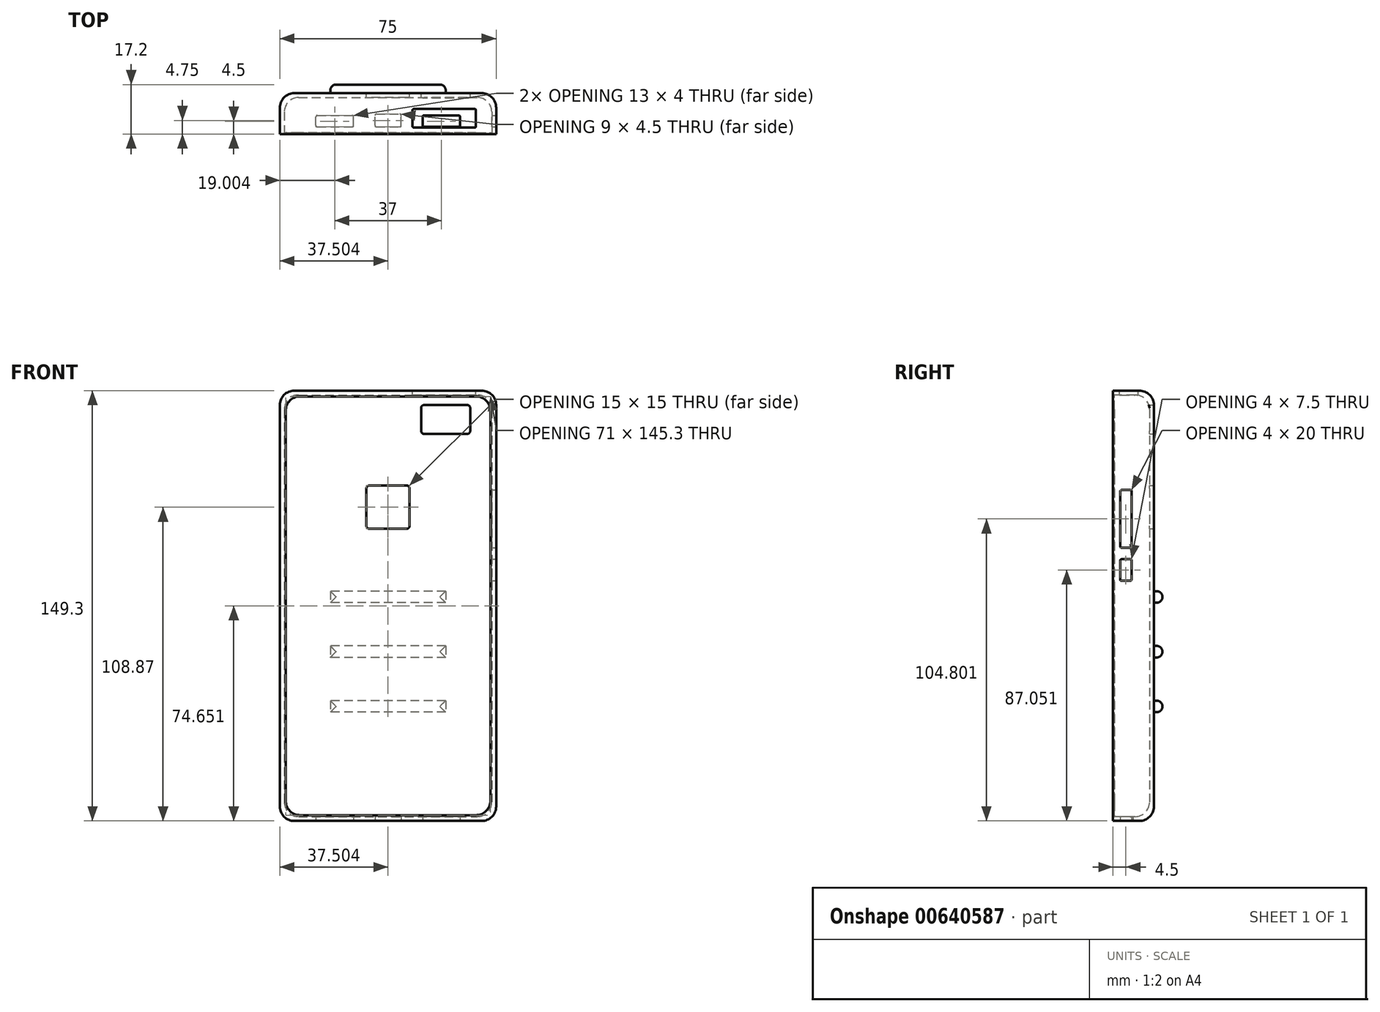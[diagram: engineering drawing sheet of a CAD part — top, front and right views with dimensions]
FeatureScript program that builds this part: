
annotation { "Feature Type Name" : "Feature", "Feature Type Description" : "" }
export const myFeature = defineFeature(function(context is Context, id is Id, definition is map)
    precondition{}
    {
        {
            var Q0;
            Q0=qCreatedBy(makeId("Front.planeOp"),FACE);
            var sketch = newSketch(context, id + "F0", { "sketchPlane" : qUnion([Q0])});
            skLineSegment(sketch, "E0.bottom", {"start": v(-56.12, 78.07) * mm, "end": v(18.88, 78.07) * mm});
            skLineSegment(sketch, "E0.top", {"start": v(-56.12, -71.23) * mm, "end": v(18.88, -71.23) * mm});
            skLineSegment(sketch, "E0.left", {"start": v(-56.12, 78.07) * mm, "end": v(-56.12, -71.23) * mm});
            skLineSegment(sketch, "E0.right", {"start": v(18.88, 78.07) * mm, "end": v(18.88, -71.23) * mm});
            skLineSegment(sketch, "E1", {"start": v(-55.06, -70.03) * mm, "end": v(-56.12, -71.23) * mm, "construction": true});
            skLineSegment(sketch, "E2", {"start": v(17.94, 76.77) * mm, "end": v(18.88, 78.07) * mm, "construction": true});
            skSolve(sketch);
        }
        {
            var Q0;
            Q0=makeQuery(id+"F0.imprint","IMPRINT",FACE,{"disambiguationData":[TD([[makeQuery(id+"F0.imprint","IMPRINT",EDGE,{"derivedFrom":sQuery(id+"F0.wireOp",EDGE,"E0.bottom")}),-1.0]])]});
            extrude(context, id + "F1", {"entities" : qUnion([Q0]), "depth" : -1.5 * mm, "offsetDistance" : 25 * mm});
        }
        {
            var Q0;
            Q0=makeQuery(id+"F1.opExtrude","CAP_FACE",FACE,{"disambiguationData":[OSD([sQuery(id+"F0.wireOp",EDGE,"E0.bottom"),sQuery(id+"F0.wireOp",EDGE,"E0.top"),sQuery(id+"F0.wireOp",EDGE,"E0.left"),sQuery(id+"F0.wireOp",EDGE,"E0.right")])],"isStart":true});
            extrude(context, id + "F2", {"entities" : qUnion([Q0]), "operationType" : NewBodyOperationType.ADD, "depth" : 12.2 * mm, "offsetDistance" : 25 * mm});
        }
        {
            var Q0;
            Q0=makeQuery(id+"F2.opExtrude","CAP_FACE",FACE,{"disambiguationData":[OSD([sQuery(id+"F0.wireOp",EDGE,"E0.bottom"),sQuery(id+"F0.wireOp",EDGE,"E0.top"),sQuery(id+"F0.wireOp",EDGE,"E0.left"),sQuery(id+"F0.wireOp",EDGE,"E0.right")])],"isStart":false});
            shell(context, id + "F3", {"entities" : qUnion([Q0]), "thickness" : 1.5 * mm});
        }
        {
            var Q0;
            {var subQ0=sQuery(id+"F0.wireOp",EDGE,"E0.top");Q0=makeQuery(id+"F2.boolean.opBoolean","MERGE",FACE,{"derivedFrom":[makeQuery(id+"F1.opExtrude","SWEPT_FACE",FACE,{"disambiguationData":[OSD([subQ0])]}),makeQuery(id+"F2.opExtrude","SWEPT_FACE",FACE,{"disambiguationData":[OSD([subQ0])]})]});}
            var sketch = newSketch(context, id + "F4", { "sketchPlane" : qUnion([Q0])});
            skLineSegment(sketch, "E3.bottom", {"start": v(-43.62, 10.2) * mm, "end": v(-30.62, 10.2) * mm});
            skLineSegment(sketch, "E3.top", {"start": v(-43.62, 6.2) * mm, "end": v(-30.62, 6.2) * mm});
            skLineSegment(sketch, "E3.left", {"start": v(-43.62, 10.2) * mm, "end": v(-43.62, 6.2) * mm});
            skLineSegment(sketch, "E3.right", {"start": v(-30.62, 10.2) * mm, "end": v(-30.62, 6.2) * mm});
            skLineSegment(sketch, "E4.bottom", {"start": v(-23.12, 10.2) * mm, "end": v(-14.12, 10.2) * mm});
            skLineSegment(sketch, "E4.top", {"start": v(-23.12, 5.7) * mm, "end": v(-14.12, 5.7) * mm});
            skLineSegment(sketch, "E4.left", {"start": v(-23.12, 10.2) * mm, "end": v(-23.12, 5.7) * mm});
            skLineSegment(sketch, "E4.right", {"start": v(-14.12, 10.2) * mm, "end": v(-14.12, 5.7) * mm});
            skLineSegment(sketch, "E5.bottom", {"start": v(-6.62, 10.2) * mm, "end": v(6.38, 10.2) * mm});
            skLineSegment(sketch, "E5.top", {"start": v(-6.62, 6.2) * mm, "end": v(6.38, 6.2) * mm});
            skLineSegment(sketch, "E5.left", {"start": v(-6.62, 10.2) * mm, "end": v(-6.62, 6.2) * mm});
            skLineSegment(sketch, "E5.right", {"start": v(6.38, 10.2) * mm, "end": v(6.38, 6.2) * mm});
            skLineSegment(sketch, "E6", {"start": v(-30.62, 10.2) * mm, "end": v(-23.12, 10.2) * mm, "construction": true});
            skLineSegment(sketch, "E7", {"start": v(-14.12, 10.2) * mm, "end": v(-6.62, 10.2) * mm, "construction": true});
            skLineSegment(sketch, "E8", {"start": v(-30.58, 10.2) * mm, "end": v(-30.58, 12.2) * mm, "construction": true});
            skLineSegment(sketch, "E9", {"start": v(6.38, 8.2) * mm, "end": v(18.88, 8.2) * mm, "construction": true});
            skLineSegment(sketch, "E10", {"start": v(-43.62, 8.2) * mm, "end": v(-56.12, 8.2) * mm, "construction": true});
            skSolve(sketch);
        }
        {
            var Q0;
            Q0=makeQuery(id+"F4.imprint","IMPRINT",FACE,{"disambiguationData":[TD([[makeQuery(id+"F4.imprint","IMPRINT",EDGE,{"derivedFrom":sQuery(id+"F4.wireOp",EDGE,"E3.bottom")}),-1.0]])]});
            var Q1;
            Q1=makeQuery(id+"F4.imprint","IMPRINT",FACE,{"disambiguationData":[TD([[makeQuery(id+"F4.imprint","IMPRINT",EDGE,{"derivedFrom":sQuery(id+"F4.wireOp",EDGE,"E4.bottom")}),-1.0]])]});
            var Q2;
            Q2=makeQuery(id+"F4.imprint","IMPRINT",FACE,{"disambiguationData":[TD([[makeQuery(id+"F4.imprint","IMPRINT",EDGE,{"derivedFrom":sQuery(id+"F4.wireOp",EDGE,"E5.bottom")}),-1.0]])]});
            var Q3;
            Q3=makeQuery(id+"F3.opShell","OFFSET_FACE",FACE,{"disambiguationData":[OSD([sQuery(id+"F0.wireOp",EDGE,"E0.top")])]});
            extrude(context, id + "F5", {"entities" : qUnion([Q0, Q1, Q2]), "operationType" : NewBodyOperationType.REMOVE, "endBound" : BoundingType.UP_TO_SURFACE, "oppositeDirection" : true, "depth" : 25 * mm, "endBoundEntityFace" : qUnion([Q3]), "offsetDistance" : 25 * mm});
        }
        {
            var Q0;
            Q0=makeQuery(id+"F5.boolean.opBoolean","COPY",EDGE,{"derivedFrom":makeQuery(id+"F5.opExtrude","SWEPT_EDGE",EDGE,{"disambiguationData":[OSD([sQuery(id+"F4.wireOp",EDGE,"E4.top"),sQuery(id+"F4.wireOp",EDGE,"E4.left")])]})});
            var Q1;
            Q1=makeQuery(id+"F5.boolean.opBoolean","COPY",EDGE,{"derivedFrom":makeQuery(id+"F5.opExtrude","SWEPT_EDGE",EDGE,{"disambiguationData":[OSD([sQuery(id+"F4.wireOp",EDGE,"E3.top"),sQuery(id+"F4.wireOp",EDGE,"E3.left")])]})});
            var Q2;
            Q2=makeQuery(id+"F5.boolean.opBoolean","COPY",EDGE,{"derivedFrom":makeQuery(id+"F5.opExtrude","SWEPT_EDGE",EDGE,{"disambiguationData":[OSD([sQuery(id+"F4.wireOp",EDGE,"E3.top"),sQuery(id+"F4.wireOp",EDGE,"E3.right")])]})});
            var Q3;
            Q3=makeQuery(id+"F5.boolean.opBoolean","COPY",EDGE,{"derivedFrom":makeQuery(id+"F5.opExtrude","SWEPT_EDGE",EDGE,{"disambiguationData":[OSD([sQuery(id+"F4.wireOp",EDGE,"E3.bottom"),sQuery(id+"F4.wireOp",EDGE,"E3.right")])]})});
            var Q4;
            Q4=makeQuery(id+"F5.boolean.opBoolean","COPY",EDGE,{"derivedFrom":makeQuery(id+"F5.opExtrude","SWEPT_EDGE",EDGE,{"disambiguationData":[OSD([sQuery(id+"F4.wireOp",EDGE,"E3.bottom"),sQuery(id+"F4.wireOp",EDGE,"E3.left")])]})});
            var Q5;
            Q5=makeQuery(id+"F5.boolean.opBoolean","COPY",EDGE,{"derivedFrom":makeQuery(id+"F5.opExtrude","CAP_EDGE",EDGE,{"disambiguationData":[OSD([sQuery(id+"F4.wireOp",EDGE,"E3.top")])],"isStart":true})});
            var Q6;
            Q6=makeQuery(id+"F5.boolean.opBoolean","COPY",EDGE,{"derivedFrom":makeQuery(id+"F5.opExtrude","SWEPT_EDGE",EDGE,{"disambiguationData":[OSD([sQuery(id+"F4.wireOp",EDGE,"E4.top"),sQuery(id+"F4.wireOp",EDGE,"E4.right")])]})});
            var Q7;
            Q7=makeQuery(id+"F5.boolean.opBoolean","COPY",EDGE,{"derivedFrom":makeQuery(id+"F5.opExtrude","SWEPT_EDGE",EDGE,{"disambiguationData":[OSD([sQuery(id+"F4.wireOp",EDGE,"E4.bottom"),sQuery(id+"F4.wireOp",EDGE,"E4.right")])]})});
            var Q8;
            Q8=makeQuery(id+"F5.boolean.opBoolean","COPY",EDGE,{"derivedFrom":makeQuery(id+"F5.opExtrude","SWEPT_EDGE",EDGE,{"disambiguationData":[OSD([sQuery(id+"F4.wireOp",EDGE,"E4.bottom"),sQuery(id+"F4.wireOp",EDGE,"E4.left")])]})});
            var Q9;
            Q9=makeQuery(id+"F5.boolean.opBoolean","COPY",EDGE,{"derivedFrom":makeQuery(id+"F5.opExtrude","CAP_EDGE",EDGE,{"disambiguationData":[OSD([sQuery(id+"F4.wireOp",EDGE,"E4.bottom")])],"isStart":true})});
            var Q10;
            Q10=makeQuery(id+"F5.boolean.opBoolean","COPY",EDGE,{"derivedFrom":makeQuery(id+"F5.opExtrude","SWEPT_EDGE",EDGE,{"disambiguationData":[OSD([sQuery(id+"F4.wireOp",EDGE,"E5.bottom"),sQuery(id+"F4.wireOp",EDGE,"E5.left")])]})});
            var Q11;
            Q11=makeQuery(id+"F5.boolean.opBoolean","COPY",EDGE,{"derivedFrom":makeQuery(id+"F5.opExtrude","CAP_EDGE",EDGE,{"disambiguationData":[OSD([sQuery(id+"F4.wireOp",EDGE,"E5.left")])],"isStart":true})});
            var Q12;
            Q12=makeQuery(id+"F5.boolean.opBoolean","COPY",EDGE,{"derivedFrom":makeQuery(id+"F5.opExtrude","SWEPT_EDGE",EDGE,{"disambiguationData":[OSD([sQuery(id+"F4.wireOp",EDGE,"E5.top"),sQuery(id+"F4.wireOp",EDGE,"E5.left")])]})});
            var Q13;
            Q13=makeQuery(id+"F5.boolean.opBoolean","COPY",EDGE,{"derivedFrom":makeQuery(id+"F5.opExtrude","SWEPT_EDGE",EDGE,{"disambiguationData":[OSD([sQuery(id+"F4.wireOp",EDGE,"E5.top"),sQuery(id+"F4.wireOp",EDGE,"E5.right")])]})});
            var Q14;
            Q14=makeQuery(id+"F5.boolean.opBoolean","COPY",EDGE,{"derivedFrom":makeQuery(id+"F5.opExtrude","SWEPT_EDGE",EDGE,{"disambiguationData":[OSD([sQuery(id+"F4.wireOp",EDGE,"E5.bottom"),sQuery(id+"F4.wireOp",EDGE,"E5.right")])]})});
            fillet(context, id + "F6", {"entities" : qUnion([Q0, Q1, Q2, Q3, Q4, Q5, Q6, Q7, Q8, Q9, Q10, Q11, Q12, Q13, Q14]), "radius" : 0.5 * mm, "tangentPropagation" : true, "allowEdgeOverflow" : false});
        }
        {
            var Q0;
            {var subQ0=sQuery(id+"F0.wireOp",EDGE,"E0.right");Q0=makeQuery(id+"F2.boolean.opBoolean","MERGE",FACE,{"derivedFrom":[makeQuery(id+"F1.opExtrude","SWEPT_FACE",FACE,{"disambiguationData":[OSD([subQ0])]}),makeQuery(id+"F2.opExtrude","SWEPT_FACE",FACE,{"disambiguationData":[OSD([subQ0])]})]});}
            var sketch = newSketch(context, id + "F7", { "sketchPlane" : qUnion([Q0])});
            skLineSegment(sketch, "E11.bottom", {"start": v(-10.2, 23.57) * mm, "end": v(-6.2, 23.57) * mm});
            skLineSegment(sketch, "E11.top", {"start": v(-10.2, 43.57) * mm, "end": v(-6.2, 43.57) * mm});
            skLineSegment(sketch, "E11.left", {"start": v(-10.2, 23.57) * mm, "end": v(-10.2, 43.57) * mm});
            skLineSegment(sketch, "E11.right", {"start": v(-6.2, 23.57) * mm, "end": v(-6.2, 43.57) * mm});
            skLineSegment(sketch, "E12", {"start": v(-8.2, 43.57) * mm, "end": v(-8.2, 78.07) * mm, "construction": true});
            skLineSegment(sketch, "E13.bottom", {"start": v(-10.2, 12.07) * mm, "end": v(-6.2, 12.07) * mm});
            skLineSegment(sketch, "E13.top", {"start": v(-10.2, 19.57) * mm, "end": v(-6.2, 19.57) * mm});
            skLineSegment(sketch, "E13.left", {"start": v(-10.2, 12.07) * mm, "end": v(-10.2, 19.57) * mm});
            skLineSegment(sketch, "E13.right", {"start": v(-6.2, 12.07) * mm, "end": v(-6.2, 19.57) * mm});
            skLineSegment(sketch, "E14", {"start": v(-10.2, 19.57) * mm, "end": v(-10.2, 23.57) * mm, "construction": true});
            skSolve(sketch);
        }
        {
            var Q0;
            {var subQ0=sQuery(id+"F0.wireOp",EDGE,"E0.bottom");Q0=makeQuery(id+"F2.boolean.opBoolean","MERGE",FACE,{"derivedFrom":[makeQuery(id+"F1.opExtrude","SWEPT_FACE",FACE,{"disambiguationData":[OSD([subQ0])]}),makeQuery(id+"F2.opExtrude","SWEPT_FACE",FACE,{"disambiguationData":[OSD([subQ0])]})]});}
            var sketch = newSketch(context, id + "F8", { "sketchPlane" : qUnion([Q0])});
            skLineSegment(sketch, "E15.bottom", {"start": v(11.88, -10.45) * mm, "end": v(-10.12, -10.45) * mm});
            skLineSegment(sketch, "E15.top", {"start": v(11.88, -3.95) * mm, "end": v(-10.12, -3.95) * mm});
            skLineSegment(sketch, "E15.left", {"start": v(11.88, -10.45) * mm, "end": v(11.88, -3.95) * mm});
            skLineSegment(sketch, "E15.right", {"start": v(-10.12, -10.45) * mm, "end": v(-10.12, -3.95) * mm});
            skSolve(sketch);
        }
        {
            var Q0;
            Q0=makeQuery(id+"F8.imprint","IMPRINT",FACE,{"disambiguationData":[TD([[makeQuery(id+"F8.imprint","IMPRINT",EDGE,{"derivedFrom":sQuery(id+"F8.wireOp",EDGE,"E15.bottom")}),-1.0]])]});
            var Q1;
            Q1=makeQuery(id+"F3.opShell","OFFSET_FACE",FACE,{"disambiguationData":[OSD([sQuery(id+"F0.wireOp",EDGE,"E0.bottom")])]});
            extrude(context, id + "F9", {"entities" : qUnion([Q0]), "operationType" : NewBodyOperationType.REMOVE, "endBound" : BoundingType.UP_TO_SURFACE, "oppositeDirection" : true, "depth" : 25 * mm, "endBoundEntityFace" : qUnion([Q1]), "offsetDistance" : 25 * mm});
        }
        {
            var Q0;
            Q0=makeQuery(id+"F9.boolean.opBoolean","COPY",EDGE,{"derivedFrom":makeQuery(id+"F9.opExtrude","SWEPT_EDGE",EDGE,{"disambiguationData":[OSD([sQuery(id+"F8.wireOp",EDGE,"E15.top"),sQuery(id+"F8.wireOp",EDGE,"E15.left")])]})});
            var Q1;
            Q1=makeQuery(id+"F9.boolean.opBoolean","COPY",EDGE,{"derivedFrom":makeQuery(id+"F9.opExtrude","SWEPT_EDGE",EDGE,{"disambiguationData":[OSD([sQuery(id+"F8.wireOp",EDGE,"E15.bottom"),sQuery(id+"F8.wireOp",EDGE,"E15.left")])]})});
            var Q2;
            Q2=makeQuery(id+"F9.boolean.opBoolean","COPY",EDGE,{"derivedFrom":makeQuery(id+"F9.opExtrude","CAP_EDGE",EDGE,{"disambiguationData":[OSD([sQuery(id+"F8.wireOp",EDGE,"E15.right")])],"isStart":true})});
            var Q3;
            Q3=makeQuery(id+"F9.boolean.opBoolean","COPY",EDGE,{"derivedFrom":makeQuery(id+"F9.opExtrude","SWEPT_EDGE",EDGE,{"disambiguationData":[OSD([sQuery(id+"F8.wireOp",EDGE,"E15.top"),sQuery(id+"F8.wireOp",EDGE,"E15.right")])]})});
            var Q4;
            Q4=makeQuery(id+"F9.boolean.opBoolean","COPY",EDGE,{"derivedFrom":makeQuery(id+"F9.opExtrude","SWEPT_EDGE",EDGE,{"disambiguationData":[OSD([sQuery(id+"F8.wireOp",EDGE,"E15.bottom"),sQuery(id+"F8.wireOp",EDGE,"E15.right")])]})});
            fillet(context, id + "F10", {"entities" : qUnion([Q0, Q1, Q2, Q3, Q4]), "radius" : 0.5 * mm, "tangentPropagation" : true, "allowEdgeOverflow" : false});
        }
        {
            var Q0;
            Q0=makeQuery(id+"F7.imprint","IMPRINT",FACE,{"disambiguationData":[TD([[makeQuery(id+"F7.imprint","IMPRINT",EDGE,{"derivedFrom":sQuery(id+"F7.wireOp",EDGE,"E11.bottom")}),1.0]])]});
            var Q1;
            Q1=makeQuery(id+"F7.imprint","IMPRINT",FACE,{"disambiguationData":[TD([[makeQuery(id+"F7.imprint","IMPRINT",EDGE,{"derivedFrom":sQuery(id+"F7.wireOp",EDGE,"E13.bottom")}),1.0]])]});
            var Q2;
            Q2=makeQuery(id+"F3.opShell","OFFSET_FACE",FACE,{"disambiguationData":[OSD([sQuery(id+"F0.wireOp",EDGE,"E0.right")])]});
            extrude(context, id + "F11", {"entities" : qUnion([Q0, Q1]), "operationType" : NewBodyOperationType.REMOVE, "endBound" : BoundingType.UP_TO_SURFACE, "oppositeDirection" : true, "depth" : 25 * mm, "endBoundEntityFace" : qUnion([Q2]), "offsetDistance" : 25 * mm});
        }
        {
            var Q0;
            Q0=makeQuery(id+"F11.boolean.opBoolean","COPY",EDGE,{"derivedFrom":makeQuery(id+"F11.opExtrude","SWEPT_EDGE",EDGE,{"disambiguationData":[OSD([sQuery(id+"F7.wireOp",EDGE,"E13.bottom"),sQuery(id+"F7.wireOp",EDGE,"E13.right")])]})});
            var Q1;
            Q1=makeQuery(id+"F11.boolean.opBoolean","COPY",EDGE,{"derivedFrom":makeQuery(id+"F11.opExtrude","SWEPT_EDGE",EDGE,{"disambiguationData":[OSD([sQuery(id+"F7.wireOp",EDGE,"E11.bottom"),sQuery(id+"F7.wireOp",EDGE,"E11.right")])]})});
            var Q2;
            Q2=makeQuery(id+"F11.boolean.opBoolean","COPY",EDGE,{"derivedFrom":makeQuery(id+"F11.opExtrude","SWEPT_EDGE",EDGE,{"disambiguationData":[OSD([sQuery(id+"F7.wireOp",EDGE,"E13.bottom"),sQuery(id+"F7.wireOp",EDGE,"E13.left")])]})});
            var Q3;
            Q3=makeQuery(id+"F11.boolean.opBoolean","COPY",EDGE,{"derivedFrom":makeQuery(id+"F11.opExtrude","SWEPT_EDGE",EDGE,{"disambiguationData":[OSD([sQuery(id+"F7.wireOp",EDGE,"E11.bottom"),sQuery(id+"F7.wireOp",EDGE,"E11.left")])]})});
            var Q4;
            Q4=makeQuery(id+"F11.boolean.opBoolean","COPY",EDGE,{"derivedFrom":makeQuery(id+"F11.opExtrude","SWEPT_EDGE",EDGE,{"disambiguationData":[OSD([sQuery(id+"F7.wireOp",EDGE,"E13.top"),sQuery(id+"F7.wireOp",EDGE,"E13.right")])]})});
            var Q5;
            Q5=makeQuery(id+"F11.boolean.opBoolean","COPY",EDGE,{"derivedFrom":makeQuery(id+"F11.opExtrude","SWEPT_EDGE",EDGE,{"disambiguationData":[OSD([sQuery(id+"F7.wireOp",EDGE,"E11.top"),sQuery(id+"F7.wireOp",EDGE,"E11.right")])]})});
            var Q6;
            Q6=makeQuery(id+"F11.boolean.opBoolean","COPY",EDGE,{"derivedFrom":makeQuery(id+"F11.opExtrude","CAP_EDGE",EDGE,{"disambiguationData":[OSD([sQuery(id+"F7.wireOp",EDGE,"E11.left")])],"isStart":true})});
            var Q7;
            Q7=makeQuery(id+"F11.boolean.opBoolean","COPY",EDGE,{"derivedFrom":makeQuery(id+"F11.opExtrude","SWEPT_EDGE",EDGE,{"disambiguationData":[OSD([sQuery(id+"F7.wireOp",EDGE,"E11.top"),sQuery(id+"F7.wireOp",EDGE,"E11.left")])]})});
            var Q8;
            Q8=makeQuery(id+"F11.boolean.opBoolean","COPY",EDGE,{"derivedFrom":makeQuery(id+"F11.opExtrude","SWEPT_EDGE",EDGE,{"disambiguationData":[OSD([sQuery(id+"F7.wireOp",EDGE,"E13.top"),sQuery(id+"F7.wireOp",EDGE,"E13.left")])]})});
            var Q9;
            Q9=makeQuery(id+"F11.boolean.opBoolean","COPY",EDGE,{"derivedFrom":makeQuery(id+"F11.opExtrude","CAP_EDGE",EDGE,{"disambiguationData":[OSD([sQuery(id+"F7.wireOp",EDGE,"E13.left")])],"isStart":true})});
            fillet(context, id + "F12", {"entities" : qUnion([Q0, Q1, Q2, Q3, Q4, Q5, Q6, Q7, Q8, Q9]), "radius" : 0.5 * mm, "tangentPropagation" : true, "allowEdgeOverflow" : false});
        }
        {
            var Q0;
            Q0=makeQuery(id+"F1.opExtrude","CAP_FACE",FACE,{"disambiguationData":[OSD([sQuery(id+"F0.wireOp",EDGE,"E0.bottom"),sQuery(id+"F0.wireOp",EDGE,"E0.top"),sQuery(id+"F0.wireOp",EDGE,"E0.left"),sQuery(id+"F0.wireOp",EDGE,"E0.right")])],"isStart":false});
            var sketch = newSketch(context, id + "F13", { "sketchPlane" : qUnion([Q0])});
            skLineSegment(sketch, "E16.bottom", {"start": v(-9.88, 73.07) * mm, "end": v(7.12, 73.07) * mm});
            skLineSegment(sketch, "E16.top", {"start": v(-9.88, 63.07) * mm, "end": v(7.12, 63.07) * mm});
            skLineSegment(sketch, "E16.left", {"start": v(-9.88, 73.07) * mm, "end": v(-9.88, 63.07) * mm});
            skLineSegment(sketch, "E16.right", {"start": v(7.12, 73.07) * mm, "end": v(7.12, 63.07) * mm});
            skLineSegment(sketch, "E17.bottom", {"start": v(11.12, 45.14) * mm, "end": v(26.12, 45.14) * mm});
            skLineSegment(sketch, "E17.top", {"start": v(11.12, 30.14) * mm, "end": v(26.12, 30.14) * mm});
            skLineSegment(sketch, "E17.left", {"start": v(11.12, 45.14) * mm, "end": v(11.12, 30.14) * mm});
            skLineSegment(sketch, "E17.right", {"start": v(26.12, 45.14) * mm, "end": v(26.12, 30.14) * mm});
            skSolve(sketch);
        }
        {
            var Q0;
            Q0=makeQuery(id+"F13.imprint","IMPRINT",FACE,{"disambiguationData":[TD([[makeQuery(id+"F13.imprint","IMPRINT",EDGE,{"derivedFrom":sQuery(id+"F13.wireOp",EDGE,"E17.bottom")}),-1.0]])]});
            var Q1;
            Q1=makeQuery(id+"F13.imprint","IMPRINT",FACE,{"disambiguationData":[TD([[makeQuery(id+"F13.imprint","IMPRINT",EDGE,{"derivedFrom":sQuery(id+"F13.wireOp",EDGE,"E16.bottom")}),-1.0]])]});
            var Q2;
            Q2=makeQuery(id+"F3.opShell","OFFSET_FACE",FACE,{"disambiguationData":[OSD([sQuery(id+"F0.wireOp",EDGE,"E0.bottom"),sQuery(id+"F0.wireOp",EDGE,"E0.top"),sQuery(id+"F0.wireOp",EDGE,"E0.left"),sQuery(id+"F0.wireOp",EDGE,"E0.right")])]});
            extrude(context, id + "F14", {"entities" : qUnion([Q0, Q1]), "operationType" : NewBodyOperationType.REMOVE, "endBound" : BoundingType.UP_TO_SURFACE, "oppositeDirection" : true, "depth" : 25 * mm, "endBoundEntityFace" : qUnion([Q2]), "offsetDistance" : 25 * mm});
        }
        {
            var Q0;
            Q0=makeQuery(id+"F14.boolean.opBoolean","COPY",EDGE,{"derivedFrom":makeQuery(id+"F14.opExtrude","SWEPT_EDGE",EDGE,{"disambiguationData":[OSD([sQuery(id+"F13.wireOp",EDGE,"E16.top"),sQuery(id+"F13.wireOp",EDGE,"E16.left")])]})});
            var Q1;
            Q1=makeQuery(id+"F14.boolean.opBoolean","COPY",EDGE,{"derivedFrom":makeQuery(id+"F14.opExtrude","SWEPT_EDGE",EDGE,{"disambiguationData":[OSD([sQuery(id+"F13.wireOp",EDGE,"E16.top"),sQuery(id+"F13.wireOp",EDGE,"E16.right")])]})});
            var Q2;
            Q2=makeQuery(id+"F14.boolean.opBoolean","COPY",EDGE,{"derivedFrom":makeQuery(id+"F14.opExtrude","SWEPT_EDGE",EDGE,{"disambiguationData":[OSD([sQuery(id+"F13.wireOp",EDGE,"E16.bottom"),sQuery(id+"F13.wireOp",EDGE,"E16.right")])]})});
            var Q3;
            Q3=makeQuery(id+"F14.boolean.opBoolean","COPY",EDGE,{"derivedFrom":makeQuery(id+"F14.opExtrude","SWEPT_EDGE",EDGE,{"disambiguationData":[OSD([sQuery(id+"F13.wireOp",EDGE,"E16.bottom"),sQuery(id+"F13.wireOp",EDGE,"E16.left")])]})});
            var Q4;
            Q4=makeQuery(id+"F14.boolean.opBoolean","COPY",EDGE,{"derivedFrom":makeQuery(id+"F14.opExtrude","CAP_EDGE",EDGE,{"disambiguationData":[OSD([sQuery(id+"F13.wireOp",EDGE,"E16.bottom")])],"isStart":true})});
            var Q5;
            Q5=makeQuery(id+"F14.boolean.opBoolean","COPY",EDGE,{"derivedFrom":makeQuery(id+"F14.opExtrude","SWEPT_EDGE",EDGE,{"disambiguationData":[OSD([sQuery(id+"F13.wireOp",EDGE,"E17.top"),sQuery(id+"F13.wireOp",EDGE,"E17.left")])]})});
            var Q6;
            Q6=makeQuery(id+"F14.boolean.opBoolean","COPY",EDGE,{"derivedFrom":makeQuery(id+"F14.opExtrude","SWEPT_EDGE",EDGE,{"disambiguationData":[OSD([sQuery(id+"F13.wireOp",EDGE,"E17.bottom"),sQuery(id+"F13.wireOp",EDGE,"E17.left")])]})});
            var Q7;
            Q7=makeQuery(id+"F14.boolean.opBoolean","COPY",EDGE,{"derivedFrom":makeQuery(id+"F14.opExtrude","SWEPT_EDGE",EDGE,{"disambiguationData":[OSD([sQuery(id+"F13.wireOp",EDGE,"E17.bottom"),sQuery(id+"F13.wireOp",EDGE,"E17.right")])]})});
            var Q8;
            Q8=makeQuery(id+"F14.boolean.opBoolean","COPY",EDGE,{"derivedFrom":makeQuery(id+"F14.opExtrude","SWEPT_EDGE",EDGE,{"disambiguationData":[OSD([sQuery(id+"F13.wireOp",EDGE,"E17.top"),sQuery(id+"F13.wireOp",EDGE,"E17.right")])]})});
            var Q9;
            Q9=makeQuery(id+"F14.boolean.opBoolean","COPY",EDGE,{"derivedFrom":makeQuery(id+"F14.opExtrude","CAP_EDGE",EDGE,{"disambiguationData":[OSD([sQuery(id+"F13.wireOp",EDGE,"E17.right")])],"isStart":true})});
            fillet(context, id + "F15", {"entities" : qUnion([Q0, Q1, Q2, Q3, Q4, Q5, Q6, Q7, Q8, Q9]), "radius" : 1 * mm, "tangentPropagation" : true, "allowEdgeOverflow" : false});
        }
        {
            var Q0;
            Q0=makeQuery(id+"F1.opExtrude","CAP_EDGE",EDGE,{"disambiguationData":[OSD([sQuery(id+"F0.wireOp",EDGE,"E0.top")])],"isStart":false});
            fillet(context, id + "F16", {"entities" : qUnion([Q0]), "radius" : 5 * mm, "tangentPropagation" : true, "allowEdgeOverflow" : false});
        }
        {
            var Q0;
            Q0=makeQuery(id+"F2.opExtrude","CAP_FACE",FACE,{"disambiguationData":[OSD([sQuery(id+"F0.wireOp",EDGE,"E0.bottom"),sQuery(id+"F0.wireOp",EDGE,"E0.top"),sQuery(id+"F0.wireOp",EDGE,"E0.left"),sQuery(id+"F0.wireOp",EDGE,"E0.right")])],"isStart":false});
            var sketch = newSketch(context, id + "F17", { "sketchPlane" : qUnion([Q0])});
            skLineSegment(sketch, "E18.bottom", {"start": v(-56.12, 78.07) * mm, "end": v(18.88, 78.07) * mm});
            skLineSegment(sketch, "E18.top", {"start": v(-56.12, -71.23) * mm, "end": v(18.88, -71.23) * mm});
            skLineSegment(sketch, "E18.left", {"start": v(-56.12, 78.07) * mm, "end": v(-56.12, -71.23) * mm});
            skLineSegment(sketch, "E18.right", {"start": v(18.88, 78.07) * mm, "end": v(18.88, -71.23) * mm});
            skLineSegment(sketch, "E19.bottom", {"start": v(16.88, -69.23) * mm, "end": v(-54.12, -69.23) * mm});
            skLineSegment(sketch, "E19.top", {"start": v(16.88, 76.07) * mm, "end": v(-54.12, 76.07) * mm});
            skLineSegment(sketch, "E19.left", {"start": v(16.88, -69.23) * mm, "end": v(16.88, 76.07) * mm});
            skLineSegment(sketch, "E19.right", {"start": v(-54.12, -69.23) * mm, "end": v(-54.12, 76.07) * mm});
            skSolve(sketch);
        }
        {
            var Q0;
            {var subQ0=sQuery(id+"F0.wireOp",EDGE,"E0.left");var subQ1=sQuery(id+"F0.wireOp",EDGE,"E0.bottom");Q0=makeQuery(id+"F2.boolean.opBoolean","MERGE",EDGE,{"derivedFrom":[makeQuery(id+"F1.opExtrude","SWEPT_EDGE",EDGE,{"disambiguationData":[OSD([subQ1,subQ0])]}),makeQuery(id+"F2.opExtrude","SWEPT_EDGE",EDGE,{"disambiguationData":[OSD([subQ1,subQ0])]})]});}
            var Q1;
            Q1=makeQuery(id+"F3.opShell","OFFSET_EDGE",EDGE,{"disambiguationData":[OSD([sQuery(id+"F0.wireOp",EDGE,"E0.bottom"),sQuery(id+"F0.wireOp",EDGE,"E0.left")])]});
            var Q2;
            {var subQ0=sQuery(id+"F0.wireOp",EDGE,"E0.right");var subQ1=sQuery(id+"F0.wireOp",EDGE,"E0.bottom");Q2=makeQuery(id+"F2.boolean.opBoolean","MERGE",EDGE,{"derivedFrom":[makeQuery(id+"F1.opExtrude","SWEPT_EDGE",EDGE,{"disambiguationData":[OSD([subQ1,subQ0])]}),makeQuery(id+"F2.opExtrude","SWEPT_EDGE",EDGE,{"disambiguationData":[OSD([subQ1,subQ0])]})]});}
            var Q3;
            Q3=makeQuery(id+"F3.opShell","OFFSET_EDGE",EDGE,{"disambiguationData":[OSD([sQuery(id+"F0.wireOp",EDGE,"E0.bottom"),sQuery(id+"F0.wireOp",EDGE,"E0.right")])]});
            var Q4;
            {var subQ0=sQuery(id+"F0.wireOp",EDGE,"E0.left");var subQ1=sQuery(id+"F0.wireOp",EDGE,"E0.top");Q4=makeQuery(id+"F2.boolean.opBoolean","MERGE",EDGE,{"derivedFrom":[makeQuery(id+"F1.opExtrude","SWEPT_EDGE",EDGE,{"disambiguationData":[OSD([subQ1,subQ0])]}),makeQuery(id+"F2.opExtrude","SWEPT_EDGE",EDGE,{"disambiguationData":[OSD([subQ1,subQ0])]})]});}
            var Q5;
            {var subQ0=sQuery(id+"F0.wireOp",EDGE,"E0.right");var subQ1=sQuery(id+"F0.wireOp",EDGE,"E0.top");Q5=makeQuery(id+"F2.boolean.opBoolean","MERGE",EDGE,{"derivedFrom":[makeQuery(id+"F1.opExtrude","SWEPT_EDGE",EDGE,{"disambiguationData":[OSD([subQ1,subQ0])]}),makeQuery(id+"F2.opExtrude","SWEPT_EDGE",EDGE,{"disambiguationData":[OSD([subQ1,subQ0])]})]});}
            var Q6;
            Q6=makeQuery(id+"F3.opShell","OFFSET_EDGE",EDGE,{"disambiguationData":[OSD([sQuery(id+"F0.wireOp",EDGE,"E0.top"),sQuery(id+"F0.wireOp",EDGE,"E0.right")])]});
            var Q7;
            Q7=makeQuery(id+"F3.opShell","OFFSET_EDGE",EDGE,{"disambiguationData":[OSD([sQuery(id+"F0.wireOp",EDGE,"E0.top"),sQuery(id+"F0.wireOp",EDGE,"E0.left")])]});
            var Q8;
            Q8=makeQuery(id+"F1.opExtrude","CAP_EDGE",EDGE,{"disambiguationData":[OSD([sQuery(id+"F0.wireOp",EDGE,"E0.bottom")])],"isStart":false});
            fillet(context, id + "F18", {"entities" : qUnion([Q0, Q1, Q2, Q3, Q4, Q5, Q6, Q7, Q8]), "radius" : 5 * mm, "tangentPropagation" : true, "allowEdgeOverflow" : false});
        }
        {
            var Q0;
            Q0 = qSketchRegion(id + "F17", true);
            extrude(context, id + "F19", {"entities" : qUnion([Q0]), "operationType" : NewBodyOperationType.ADD, "depth" : 0.5 * mm, "offsetDistance" : 25 * mm});
        }
        {
            var Q0;
            Q0=makeQuery(id+"F19.opExtrude","SWEPT_EDGE",EDGE,{"disambiguationData":[OSD([sQuery(id+"F17.wireOp",EDGE,"E18.top"),sQuery(id+"F17.wireOp",EDGE,"E18.left")])]});
            var Q1;
            Q1=makeQuery(id+"F19.opExtrude","SWEPT_EDGE",EDGE,{"disambiguationData":[OSD([sQuery(id+"F17.wireOp",EDGE,"E19.bottom"),sQuery(id+"F17.wireOp",EDGE,"E19.right")])]});
            var Q2;
            Q2=makeQuery(id+"F19.opExtrude","SWEPT_EDGE",EDGE,{"disambiguationData":[OSD([sQuery(id+"F17.wireOp",EDGE,"E18.top"),sQuery(id+"F17.wireOp",EDGE,"E18.right")])]});
            var Q3;
            Q3=makeQuery(id+"F19.opExtrude","SWEPT_EDGE",EDGE,{"disambiguationData":[OSD([sQuery(id+"F17.wireOp",EDGE,"E19.bottom"),sQuery(id+"F17.wireOp",EDGE,"E19.left")])]});
            var Q4;
            Q4=makeQuery(id+"F19.opExtrude","SWEPT_EDGE",EDGE,{"disambiguationData":[OSD([sQuery(id+"F17.wireOp",EDGE,"E18.bottom"),sQuery(id+"F17.wireOp",EDGE,"E18.right")])]});
            var Q5;
            Q5=makeQuery(id+"F19.opExtrude","SWEPT_EDGE",EDGE,{"disambiguationData":[OSD([sQuery(id+"F17.wireOp",EDGE,"E19.top"),sQuery(id+"F17.wireOp",EDGE,"E19.left")])]});
            var Q6;
            Q6=makeQuery(id+"F19.opExtrude","SWEPT_EDGE",EDGE,{"disambiguationData":[OSD([sQuery(id+"F17.wireOp",EDGE,"E18.bottom"),sQuery(id+"F17.wireOp",EDGE,"E18.left")])]});
            var Q7;
            Q7=makeQuery(id+"F19.opExtrude","SWEPT_EDGE",EDGE,{"disambiguationData":[OSD([sQuery(id+"F17.wireOp",EDGE,"E19.top"),sQuery(id+"F17.wireOp",EDGE,"E19.right")])]});
            fillet(context, id + "F20", {"entities" : qUnion([Q0, Q1, Q2, Q3, Q4, Q5, Q6, Q7]), "radius" : 5 * mm, "tangentPropagation" : true, "allowEdgeOverflow" : false});
        }
        {
            var Q0;
            Q0=makeQuery(id+"F1.opExtrude","CAP_FACE",FACE,{"disambiguationData":[OSD([sQuery(id+"F0.wireOp",EDGE,"E0.bottom"),sQuery(id+"F0.wireOp",EDGE,"E0.top"),sQuery(id+"F0.wireOp",EDGE,"E0.left"),sQuery(id+"F0.wireOp",EDGE,"E0.right")])],"isStart":false});
            var sketch = newSketch(context, id + "F21", { "sketchPlane" : qUnion([Q0])});
            skLineSegment(sketch, "E20.bottom", {"start": v(-1.38, 8.5) * mm, "end": v(38.62, 8.5) * mm});
            skLineSegment(sketch, "E20.top", {"start": v(-1.38, 4.5) * mm, "end": v(38.62, 4.5) * mm});
            skLineSegment(sketch, "E20.left", {"start": v(-1.38, 8.5) * mm, "end": v(-1.38, 4.5) * mm});
            skLineSegment(sketch, "E20.right", {"start": v(38.62, 8.5) * mm, "end": v(38.62, 4.5) * mm});
            skLineSegment(sketch, "E21.bottom", {"start": v(-1.38, -10.5) * mm, "end": v(38.62, -10.5) * mm});
            skLineSegment(sketch, "E21.top", {"start": v(-1.38, -14.5) * mm, "end": v(38.62, -14.5) * mm});
            skLineSegment(sketch, "E21.left", {"start": v(-1.38, -10.5) * mm, "end": v(-1.38, -14.5) * mm});
            skLineSegment(sketch, "E21.right", {"start": v(38.62, -10.5) * mm, "end": v(38.62, -14.5) * mm});
            skLineSegment(sketch, "E22.bottom", {"start": v(-1.38, -29.5) * mm, "end": v(38.62, -29.5) * mm});
            skLineSegment(sketch, "E22.top", {"start": v(-1.38, -33.5) * mm, "end": v(38.62, -33.5) * mm});
            skLineSegment(sketch, "E22.left", {"start": v(-1.38, -29.5) * mm, "end": v(-1.38, -33.5) * mm});
            skLineSegment(sketch, "E22.right", {"start": v(38.62, -29.5) * mm, "end": v(38.62, -33.5) * mm});
            skSolve(sketch);
        }
        {
            var Q0;
            Q0=makeQuery(id+"F21.imprint","IMPRINT",FACE,{"disambiguationData":[TD([[makeQuery(id+"F21.imprint","IMPRINT",EDGE,{"derivedFrom":sQuery(id+"F21.wireOp",EDGE,"E22.bottom")}),-1.0]])]});
            var Q1;
            Q1=makeQuery(id+"F21.imprint","IMPRINT",FACE,{"disambiguationData":[TD([[makeQuery(id+"F21.imprint","IMPRINT",EDGE,{"derivedFrom":sQuery(id+"F21.wireOp",EDGE,"E21.bottom")}),-1.0]])]});
            var Q2;
            Q2=makeQuery(id+"F21.imprint","IMPRINT",FACE,{"disambiguationData":[TD([[makeQuery(id+"F21.imprint","IMPRINT",EDGE,{"derivedFrom":sQuery(id+"F21.wireOp",EDGE,"E20.bottom")}),-1.0]])]});
            extrude(context, id + "F22", {"entities" : qUnion([Q0, Q1, Q2]), "operationType" : NewBodyOperationType.ADD, "depth" : 3 * mm, "offsetDistance" : 25 * mm});
        }
        {
            var Q0;
            Q0=makeQuery(id+"F22.opExtrude","CAP_EDGE",EDGE,{"disambiguationData":[OSD([sQuery(id+"F21.wireOp",EDGE,"E20.top")])],"isStart":false});
            var Q1;
            Q1=makeQuery(id+"F22.opExtrude","CAP_EDGE",EDGE,{"disambiguationData":[OSD([sQuery(id+"F21.wireOp",EDGE,"E21.top")])],"isStart":false});
            var Q2;
            Q2=makeQuery(id+"F22.opExtrude","CAP_EDGE",EDGE,{"disambiguationData":[OSD([sQuery(id+"F21.wireOp",EDGE,"E22.top")])],"isStart":false});
            var Q3;
            Q3=makeQuery(id+"F22.opExtrude","CAP_EDGE",EDGE,{"disambiguationData":[OSD([sQuery(id+"F21.wireOp",EDGE,"E22.left")])],"isStart":false});
            var Q4;
            Q4=makeQuery(id+"F22.opExtrude","CAP_EDGE",EDGE,{"disambiguationData":[OSD([sQuery(id+"F21.wireOp",EDGE,"E21.left")])],"isStart":false});
            var Q5;
            Q5=makeQuery(id+"F22.opExtrude","CAP_EDGE",EDGE,{"disambiguationData":[OSD([sQuery(id+"F21.wireOp",EDGE,"E20.left")])],"isStart":false});
            var Q6;
            Q6=makeQuery(id+"F22.opExtrude","CAP_EDGE",EDGE,{"disambiguationData":[OSD([sQuery(id+"F21.wireOp",EDGE,"E20.bottom")])],"isStart":false});
            var Q7;
            Q7=makeQuery(id+"F22.opExtrude","CAP_EDGE",EDGE,{"disambiguationData":[OSD([sQuery(id+"F21.wireOp",EDGE,"E21.bottom")])],"isStart":false});
            var Q8;
            Q8=makeQuery(id+"F22.opExtrude","CAP_EDGE",EDGE,{"disambiguationData":[OSD([sQuery(id+"F21.wireOp",EDGE,"E22.bottom")])],"isStart":false});
            var Q9;
            Q9=makeQuery(id+"F22.opExtrude","CAP_EDGE",EDGE,{"disambiguationData":[OSD([sQuery(id+"F21.wireOp",EDGE,"E20.right")])],"isStart":false});
            var Q10;
            Q10=makeQuery(id+"F22.opExtrude","CAP_EDGE",EDGE,{"disambiguationData":[OSD([sQuery(id+"F21.wireOp",EDGE,"E21.right")])],"isStart":false});
            var Q11;
            Q11=makeQuery(id+"F22.opExtrude","CAP_EDGE",EDGE,{"disambiguationData":[OSD([sQuery(id+"F21.wireOp",EDGE,"E22.right")])],"isStart":false});
            fillet(context, id + "F23", {"entities" : qUnion([Q0, Q1, Q2, Q3, Q4, Q5, Q6, Q7, Q8, Q9, Q10, Q11]), "radius" : 2 * mm, "tangentPropagation" : true, "allowEdgeOverflow" : false});
        }
        {
            var Q0;
            {var subQ0=sQuery(id+"F0.wireOp",EDGE,"E0.right");Q0=makeQuery(id+"F3.opShell","OFFSET_EDGE",EDGE,{"disambiguationData":[OSD([subQ0]),TDD([makeQuery(id+"F1.opExtrude","CAP_EDGE",EDGE,{"disambiguationData":[OSD([subQ0])],"isStart":false})])]});}
            fillet(context, id + "F24", {"entities" : qUnion([Q0]), "radius" : 5 * mm, "tangentPropagation" : true, "allowEdgeOverflow" : false});
        }
    });
